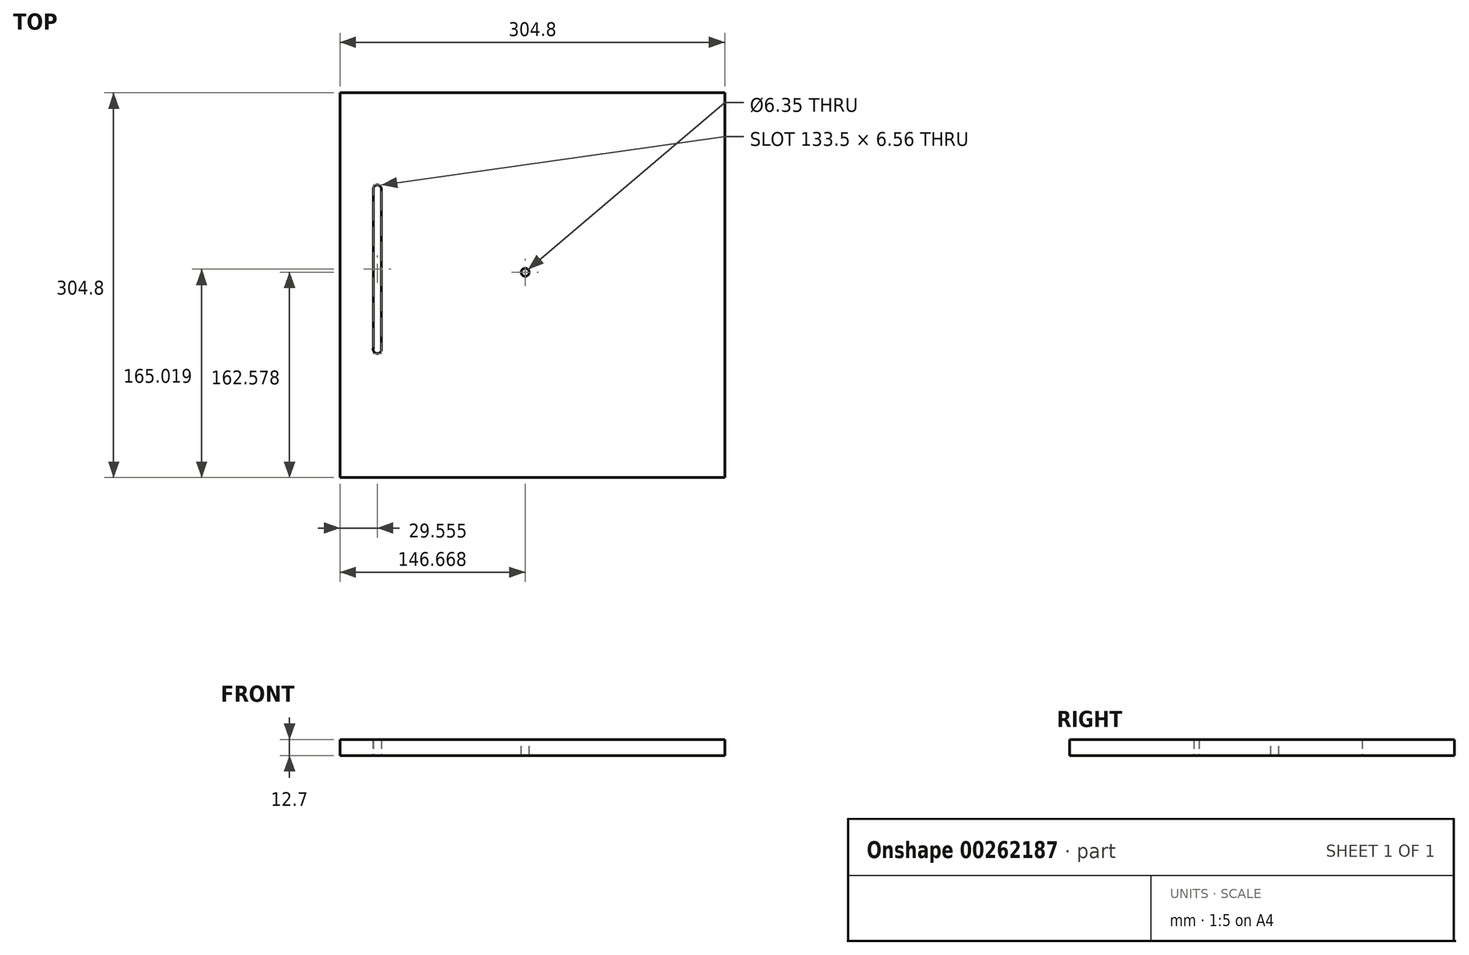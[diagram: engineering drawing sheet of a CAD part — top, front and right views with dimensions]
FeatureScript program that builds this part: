
annotation { "Feature Type Name" : "Feature", "Feature Type Description" : "" }
export const myFeature = defineFeature(function(context is Context, id is Id, definition is map)
    precondition{}
    {
        {
            var Q0;
            Q0=qCreatedBy(makeId("Top.planeOp"),FACE);
            var sketch = newSketch(context, id + "F0", { "sketchPlane" : qUnion([Q0])});
            skLineSegment(sketch, "E0.bottom", {"start": v(-154.02, 180.36) * mm, "end": v(150.78, 180.36) * mm});
            skLineSegment(sketch, "E0.top", {"start": v(-154.02, -124.44) * mm, "end": v(150.78, -124.44) * mm});
            skLineSegment(sketch, "E0.left", {"start": v(-154.02, 180.36) * mm, "end": v(-154.02, -124.44) * mm});
            skLineSegment(sketch, "E0.right", {"start": v(150.78, 180.36) * mm, "end": v(150.78, -124.44) * mm});
            skPoint(sketch, "E1", {"position": v(-127.64, 104.16) * mm});
            skLineSegment(sketch, "E2.left", {"start": v(-127.64, 104.16) * mm, "end": v(-127.64, -22.84) * mm});
            skLineSegment(sketch, "E2.right", {"start": v(-121.3, 104.16) * mm, "end": v(-121.3, -22.84) * mm});
            skArc(sketch, "E3", {"start": v(-121.3, 104.16) * mm, "mid": v(-124.47, 107.33) * mm, "end": v(-127.64, 104.16) * mm});
            skPoint(sketch, "E4.start.orphan", {"position": v(-127.64, -22.84) * mm});
            skArc(sketch, "E5", {"start": v(-127.64, -21.85) * mm, "mid": v(-124.47, -26.17) * mm, "end": v(-121.3, -21.85) * mm});
            skSolve(sketch);
        }
        {
            var Q0;
            Q0=makeQuery(id+"F0.imprint","IMPRINT",FACE,{"disambiguationData":[TD([[makeQuery(id+"F0.imprint","IMPRINT",EDGE,{"derivedFrom":sQuery(id+"F0.wireOp",EDGE,"E0.bottom")}),-1.0]])]});
            extrude(context, id + "F1", {"entities" : qUnion([Q0]), "depth" : 12.7 * mm});
        }
        {
            var Q0;
            Q0=makeQuery(id+"F1.opExtrude","CAP_FACE",FACE,{"disambiguationData":[OSD([sQuery(id+"F0.wireOp",EDGE,"E0.bottom"),sQuery(id+"F0.wireOp",EDGE,"E0.top"),sQuery(id+"F0.wireOp",EDGE,"E0.left"),sQuery(id+"F0.wireOp",EDGE,"E0.right"),sQuery(id+"F0.wireOp",EDGE,"E2.left"),sQuery(id+"F0.wireOp",EDGE,"E2.right"),sQuery(id+"F0.wireOp",EDGE,"E3"),sQuery(id+"F0.wireOp",EDGE,"E5")])],"isStart":false});
            var sketch = newSketch(context, id + "F2", { "sketchPlane" : qUnion([Q0])});
            skCircle(sketch, "E6", {"center": v(-7.35, 38.14) * mm, "radius": 17.87 * mm});
            skSolve(sketch);
        }
        {
            var Q0;
            Q0=sQuery(id+"F2.wireOp",VERTEX,"E6.center");
            var Q1;
            Q1=makeQuery(id+"F1.opExtrude","SWEPT_BODY",BODY,{"disambiguationData":[OSD([sQuery(id+"F0.wireOp",EDGE,"E0.bottom"),sQuery(id+"F0.wireOp",EDGE,"E0.top"),sQuery(id+"F0.wireOp",EDGE,"E0.left"),sQuery(id+"F0.wireOp",EDGE,"E0.right"),sQuery(id+"F0.wireOp",EDGE,"E2.left"),sQuery(id+"F0.wireOp",EDGE,"E2.right"),sQuery(id+"F0.wireOp",EDGE,"E3"),sQuery(id+"F0.wireOp",EDGE,"E5")])]});
            hole(context, id + "F3", {"style" : HoleStyle.SIMPLE, "endStyle" : HoleEndStyle.THROUGH, "holeDiameter" : 6.35 * mm, "tappedDepth" : 12.7 * mm, "tapClearance" : 3, "locations" : qUnion([Q0]), "scope" : qUnion([Q1])});
        }
    });
